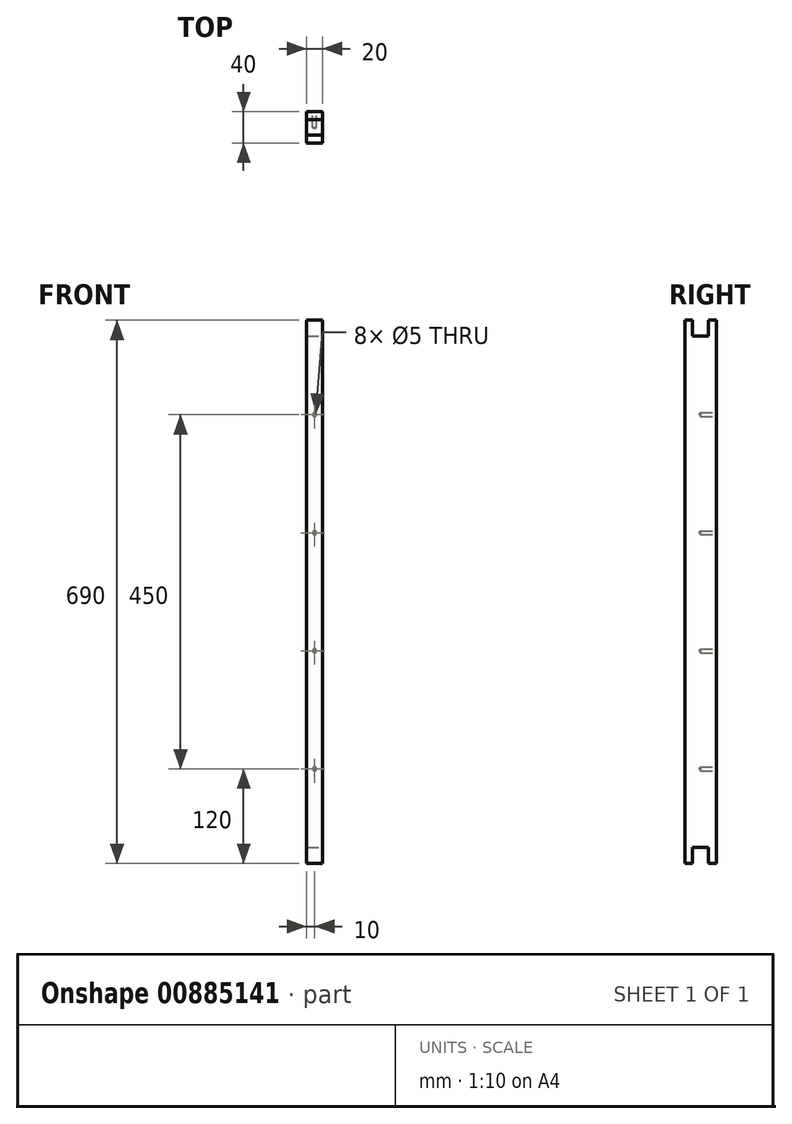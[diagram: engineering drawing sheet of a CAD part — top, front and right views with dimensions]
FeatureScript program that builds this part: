
annotation { "Feature Type Name" : "Feature", "Feature Type Description" : "" }
export const myFeature = defineFeature(function(context is Context, id is Id, definition is map)
    precondition{}
    {
        {
            var Q0;
            Q0=qCreatedBy(makeId("Top.planeOp"),FACE);
            var sketch = newSketch(context, id + "F0", { "sketchPlane" : qUnion([Q0])});
            skLineSegment(sketch, "E0.bottom", {"start": v(-10, -20) * mm, "end": v(10, -20) * mm});
            skLineSegment(sketch, "E0.top", {"start": v(-10, 20) * mm, "end": v(10, 20) * mm});
            skLineSegment(sketch, "E0.left", {"start": v(-10, -20) * mm, "end": v(-10, 20) * mm});
            skLineSegment(sketch, "E0.right", {"start": v(10, -20) * mm, "end": v(10, 20) * mm});
            skPoint(sketch, "E0.middle", {"position": v(0, 0) * mm});
            skSolve(sketch);
        }
        {
            var Q0;
            Q0=makeQuery(id+"F0.imprint","IMPRINT",FACE,{"disambiguationData":[TD([[makeQuery(id+"F0.imprint","IMPRINT",EDGE,{"derivedFrom":sQuery(id+"F0.wireOp",EDGE,"E0.bottom")}),1.0]])]});
            extrude(context, id + "F1", {"entities" : qUnion([Q0]), "depth" : 690 * mm, "offsetDistance" : 25.4 * mm});
        }
        {
            var Q0;
            Q0=makeQuery(id+"F1.opExtrude","SWEPT_FACE",FACE,{"disambiguationData":[OSD([sQuery(id+"F0.wireOp",EDGE,"E0.top")])]});
            var sketch = newSketch(context, id + "F2", { "sketchPlane" : qUnion([Q0])});
            skCircle(sketch, "E1", {"center": v(0, 570) * mm, "radius": 2.5 * mm});
            skCircle(sketch, "E2", {"center": v(0, 420) * mm, "radius": 2.5 * mm});
            skCircle(sketch, "E3", {"center": v(0, 270) * mm, "radius": 2.5 * mm});
            skCircle(sketch, "E4", {"center": v(0, 120) * mm, "radius": 2.5 * mm});
            skSolve(sketch);
        }
        {
            var Q0;
            Q0=sQuery(id+"F2.wireOp",VERTEX,"E1.center");
            var Q1;
            Q1=sQuery(id+"F2.wireOp",VERTEX,"E2.center");
            var Q2;
            Q2=sQuery(id+"F2.wireOp",VERTEX,"E3.center");
            var Q3;
            Q3=sQuery(id+"F2.wireOp",VERTEX,"E4.center");
            var Q4;
            Q4=makeQuery(id+"F1.opExtrude","SWEPT_BODY",BODY,{"disambiguationData":[OSD([sQuery(id+"F0.wireOp",EDGE,"E0.bottom"),sQuery(id+"F0.wireOp",EDGE,"E0.top"),sQuery(id+"F0.wireOp",EDGE,"E0.left"),sQuery(id+"F0.wireOp",EDGE,"E0.right")])]});
            hole(context, id + "F3", {"style" : HoleStyle.SIMPLE, "endStyle" : HoleEndStyle.BLIND, "holeDiameter" : 5 * mm, "majorDiameter" : 6.35 * mm, "holeDepth" : 20 * mm, "isTappedThrough" : true, "tappedDepth" : 12.7 * mm, "tapClearance" : 3, "locations" : qUnion([Q0, Q1, Q2, Q3]), "scope" : qUnion([Q4])});
        }
        {
            var Q0;
            Q0=makeQuery(id+"F1.opExtrude","SWEPT_FACE",FACE,{"disambiguationData":[OSD([sQuery(id+"F0.wireOp",EDGE,"E0.right")])]});
            var sketch = newSketch(context, id + "F4", { "sketchPlane" : qUnion([Q0])});
            skLineSegment(sketch, "E5.bottom", {"start": v(-10, 690) * mm, "end": v(10, 690) * mm});
            skLineSegment(sketch, "E5.top", {"start": v(-10, 670) * mm, "end": v(10, 670) * mm});
            skLineSegment(sketch, "E5.left", {"start": v(-10, 690) * mm, "end": v(-10, 670) * mm});
            skLineSegment(sketch, "E5.right", {"start": v(10, 690) * mm, "end": v(10, 670) * mm});
            skSolve(sketch);
        }
        {
            var Q0;
            Q0=makeQuery(id+"F4.imprint","IMPRINT",FACE,{"disambiguationData":[TD([[makeQuery(id+"F4.imprint","IMPRINT",EDGE,{"derivedFrom":sQuery(id+"F4.wireOp",EDGE,"E5.bottom")}),-1.0]])]});
            extrude(context, id + "F5", {"entities" : qUnion([Q0]), "operationType" : NewBodyOperationType.REMOVE, "oppositeDirection" : true, "depth" : 66.8 * mm, "offsetDistance" : 25 * mm});
        }
        {
            var Q0;
            Q0=makeQuery(id+"F1.opExtrude","SWEPT_FACE",FACE,{"disambiguationData":[OSD([sQuery(id+"F0.wireOp",EDGE,"E0.right")])]});
            var sketch = newSketch(context, id + "F6", { "sketchPlane" : qUnion([Q0])});
            skLineSegment(sketch, "E6.bottom", {"start": v(-10, 0) * mm, "end": v(10, 0) * mm});
            skLineSegment(sketch, "E6.top", {"start": v(-10, 20) * mm, "end": v(10, 20) * mm});
            skLineSegment(sketch, "E6.left", {"start": v(-10, 0) * mm, "end": v(-10, 20) * mm});
            skLineSegment(sketch, "E6.right", {"start": v(10, 0) * mm, "end": v(10, 20) * mm});
            skSolve(sketch);
        }
        {
            var Q0;
            Q0=makeQuery(id+"F6.imprint","IMPRINT",FACE,{"disambiguationData":[TD([[makeQuery(id+"F6.imprint","IMPRINT",EDGE,{"derivedFrom":sQuery(id+"F6.wireOp",EDGE,"E6.bottom")}),1.0]])]});
            extrude(context, id + "F7", {"entities" : qUnion([Q0]), "operationType" : NewBodyOperationType.REMOVE, "oppositeDirection" : true, "depth" : 25 * mm, "offsetDistance" : 25 * mm});
        }
        {
            var Q0;
            Q0=makeQuery(id+"F1.opExtrude","SWEPT_BODY",BODY,{"disambiguationData":[OSD([sQuery(id+"F0.wireOp",EDGE,"E0.bottom"),sQuery(id+"F0.wireOp",EDGE,"E0.top"),sQuery(id+"F0.wireOp",EDGE,"E0.left"),sQuery(id+"F0.wireOp",EDGE,"E0.right")])]});
            transform(context, id + "F8", {"entities" : qUnion([Q0]), "transformType" : TransformType.TRANSLATION_3D, "dx" : 0 * mm, "dy" : 0 * mm, "dz" : 0 * mm, "makeCopy" : true});
        }
        {
            var Q0;
            Q0=makeQuery(id+"F8.opPattern","COPY",BODY,{"derivedFrom":makeQuery(id+"F1.opExtrude","SWEPT_BODY",BODY,{"disambiguationData":[OSD([sQuery(id+"F0.wireOp",EDGE,"E0.bottom"),sQuery(id+"F0.wireOp",EDGE,"E0.top"),sQuery(id+"F0.wireOp",EDGE,"E0.left"),sQuery(id+"F0.wireOp",EDGE,"E0.right")])]}),"instanceName":"1"});
            deleteBodies(context, id + "F9", {"entities" : qUnion([Q0])});
        }
    });
